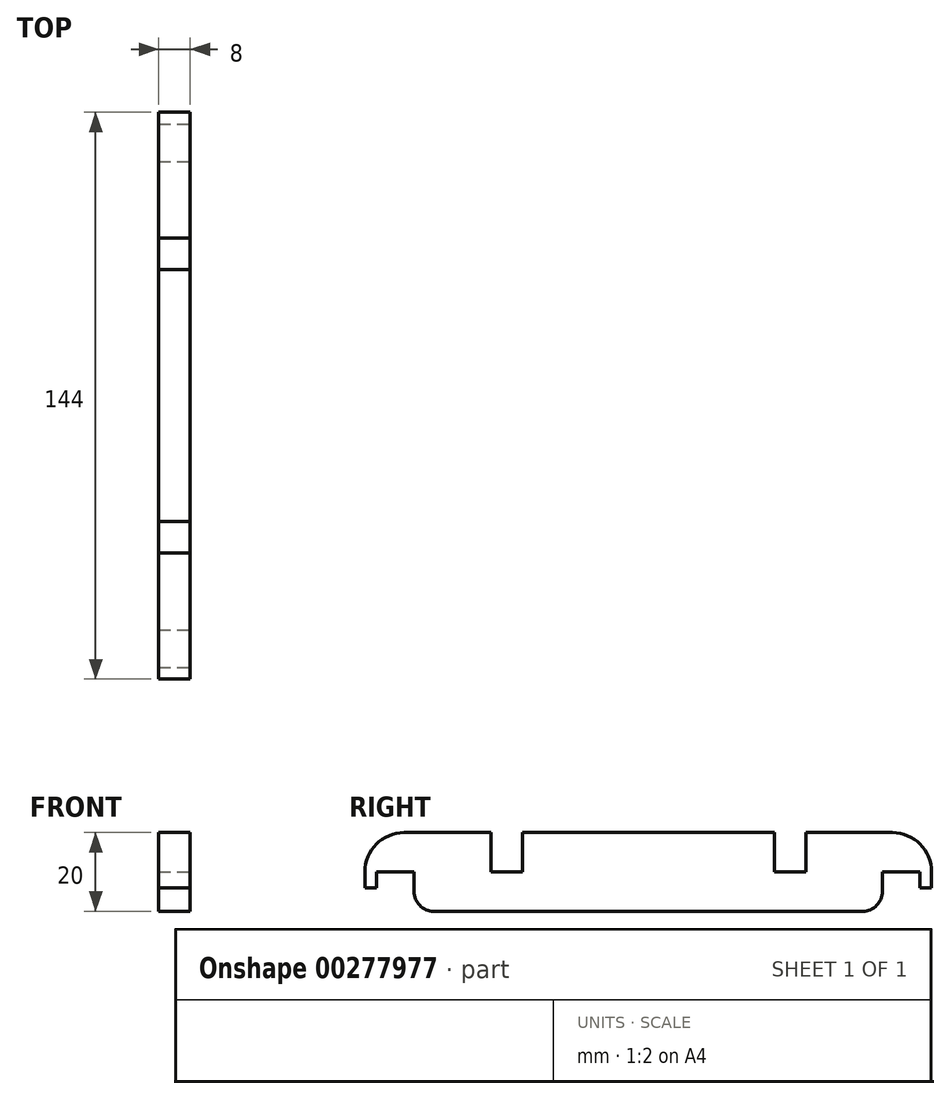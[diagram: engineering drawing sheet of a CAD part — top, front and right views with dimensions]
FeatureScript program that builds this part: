
annotation { "Feature Type Name" : "Feature", "Feature Type Description" : "" }
export const myFeature = defineFeature(function(context is Context, id is Id, definition is map)
    precondition{}
    {
        {
            var Q0;
            Q0=qCreatedBy(makeId("Right.planeOp"),FACE);
            var sketch = newSketch(context, id + "F0", { "sketchPlane" : qUnion([Q0])});
            skLineSegment(sketch, "E0", {"start": v(-49.9, 202.52) * mm, "end": v(-49.9, 222.52) * mm});
            skLineSegment(sketch, "E1", {"start": v(-49.9, 222.52) * mm, "end": v(-39.9, 222.52) * mm});
            skLineSegment(sketch, "E2", {"start": v(-39.9, 222.52) * mm, "end": v(-39.9, 212.52) * mm});
            skLineSegment(sketch, "E3", {"start": v(-39.9, 212.52) * mm, "end": v(-31.9, 212.52) * mm});
            skLineSegment(sketch, "E4", {"start": v(-31.9, 212.52) * mm, "end": v(-31.9, 222.52) * mm});
            skLineSegment(sketch, "E5", {"start": v(-31.9, 222.52) * mm, "end": v(-21.9, 222.52) * mm});
            skLineSegment(sketch, "E6", {"start": v(-21.9, 222.52) * mm, "end": v(-21.9, 212.52) * mm});
            skLineSegment(sketch, "E7", {"start": v(-101.12, 185.03) * mm, "end": v(-69.12, 185.03) * mm});
            skLineSegment(sketch, "E8", {"start": v(42.88, 185.03) * mm, "end": v(42.88, 171.03) * mm});
            skLineSegment(sketch, "E9", {"start": v(42.88, 171.03) * mm, "end": v(39.88, 171.03) * mm});
            skLineSegment(sketch, "E10", {"start": v(39.88, 171.03) * mm, "end": v(39.88, 175.03) * mm});
            skLineSegment(sketch, "E11", {"start": v(39.88, 175.03) * mm, "end": v(30.38, 175.03) * mm});
            skLineSegment(sketch, "E12", {"start": v(30.38, 175.03) * mm, "end": v(30.38, 165.03) * mm});
            skLineSegment(sketch, "E13", {"start": v(-101.12, 185.03) * mm, "end": v(-101.12, 171.03) * mm});
            skLineSegment(sketch, "E14", {"start": v(-101.12, 171.03) * mm, "end": v(-98.12, 171.03) * mm});
            skLineSegment(sketch, "E15", {"start": v(-98.12, 171.03) * mm, "end": v(-98.12, 175.03) * mm});
            skLineSegment(sketch, "E16", {"start": v(-98.12, 175.03) * mm, "end": v(-88.62, 175.03) * mm});
            skLineSegment(sketch, "E17", {"start": v(-88.62, 175.03) * mm, "end": v(-88.62, 165.03) * mm});
            skLineSegment(sketch, "E18", {"start": v(-88.62, 165.03) * mm, "end": v(30.38, 165.03) * mm});
            skLineSegment(sketch, "E19", {"start": v(-69.12, 185.03) * mm, "end": v(-69.12, 175.03) * mm});
            skLineSegment(sketch, "E20", {"start": v(-69.12, 175.03) * mm, "end": v(-61.12, 175.03) * mm});
            skLineSegment(sketch, "E21", {"start": v(-61.12, 175.03) * mm, "end": v(-61.12, 185.03) * mm});
            skLineSegment(sketch, "E22", {"start": v(10.88, 185.03) * mm, "end": v(10.88, 175.03) * mm});
            skLineSegment(sketch, "E23", {"start": v(10.88, 175.03) * mm, "end": v(2.88, 175.03) * mm});
            skLineSegment(sketch, "E24", {"start": v(2.88, 175.03) * mm, "end": v(2.88, 185.03) * mm});
            skLineSegment(sketch, "E25.trimOffspring", {"start": v(-61.12, 185.03) * mm, "end": v(2.88, 185.03) * mm});
            skLineSegment(sketch, "E26.trimOffspring", {"start": v(10.88, 185.03) * mm, "end": v(42.88, 185.03) * mm});
            skSolve(sketch);
        }
        {
            var Q0;
            Q0=qSketchRegion(id+"F0",true);
            extrude(context, id + "F1", {"entities" : qUnion([Q0]), "oppositeDirection" : true, "depth" : 8 * mm});
        }
        {
            var Q0;
            Q0=makeQuery(id+"F1.opExtrude","SWEPT_EDGE",EDGE,{"disambiguationData":[OSD([sQuery(id+"F0.wireOp",EDGE,"E7"),sQuery(id+"F0.wireOp",EDGE,"E13")])]});
            var Q1;
            Q1=makeQuery(id+"F1.opExtrude","SWEPT_EDGE",EDGE,{"disambiguationData":[OSD([sQuery(id+"F0.wireOp",EDGE,"E8"),sQuery(id+"F0.wireOp",EDGE,"E26.trimOffspring")])]});
            fillet(context, id + "F2", {"entities" : qUnion([Q0, Q1]), "radius" : 10 * mm, "tangentPropagation" : true, "allowEdgeOverflow" : false});
        }
        {
            var Q0;
            Q0=makeQuery(id+"F1.opExtrude","SWEPT_EDGE",EDGE,{"disambiguationData":[OSD([sQuery(id+"F0.wireOp",EDGE,"E17"),sQuery(id+"F0.wireOp",EDGE,"E18")])]});
            var Q1;
            Q1=makeQuery(id+"F1.opExtrude","SWEPT_EDGE",EDGE,{"disambiguationData":[OSD([sQuery(id+"F0.wireOp",EDGE,"E12"),sQuery(id+"F0.wireOp",EDGE,"E18")])]});
            fillet(context, id + "F3", {"entities" : qUnion([Q0, Q1]), "radius" : 5 * mm, "tangentPropagation" : true, "allowEdgeOverflow" : false});
        }
    });
